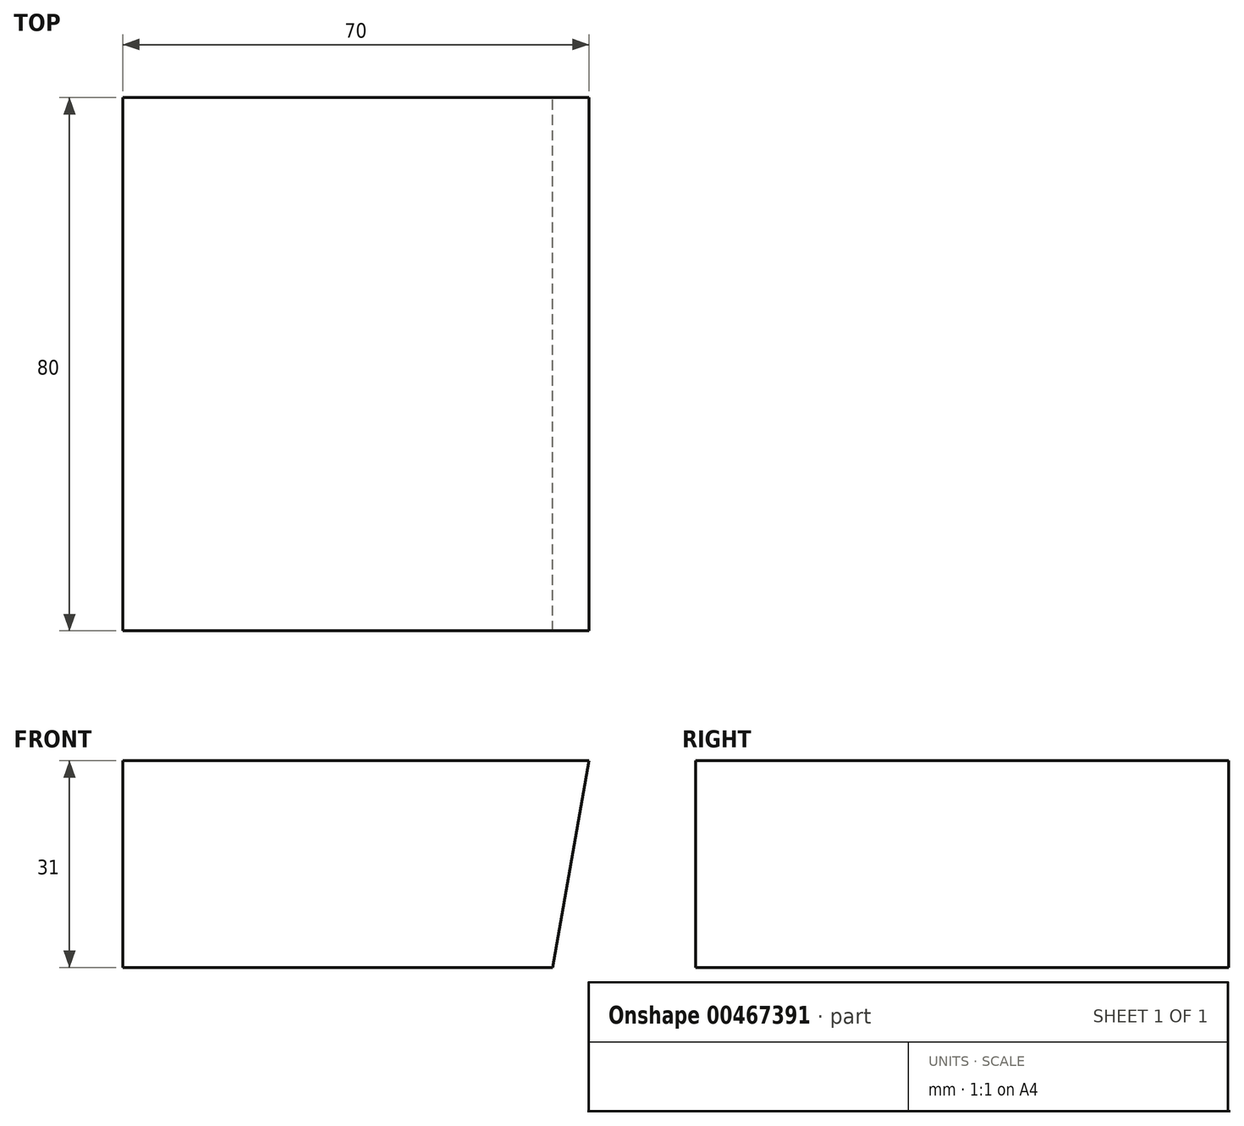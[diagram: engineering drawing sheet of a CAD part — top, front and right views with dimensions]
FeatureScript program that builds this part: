
annotation { "Feature Type Name" : "Feature", "Feature Type Description" : "" }
export const myFeature = defineFeature(function(context is Context, id is Id, definition is map)
    precondition{}
    {
        {
            var Q0;
            Q0=qCreatedBy(makeId("Front.planeOp"),FACE);
            var sketch = newSketch(context, id + "F0", { "sketchPlane" : qUnion([Q0])});
            skLineSegment(sketch, "E0.bottom", {"start": v(-34.34, -15.5) * mm, "end": v(30.2, -15.5) * mm});
            skLineSegment(sketch, "E0.top", {"start": v(-34.34, 15.5) * mm, "end": v(35.66, 15.5) * mm});
            skLineSegment(sketch, "E0.left", {"start": v(-34.34, -15.5) * mm, "end": v(-34.34, 15.5) * mm});
            skLineSegment(sketch, "E1", {"start": v(30.2, -15.5) * mm, "end": v(35.66, 15.5) * mm});
            skSolve(sketch);
        }
        {
            var Q0;
            Q0 = qSketchRegion(id + "F0", true);
            extrude(context, id + "F1", {"entities" : qUnion([Q0]), "endBound" : BoundingType.SYMMETRIC, "depth" : 80 * mm});
        }
    });
